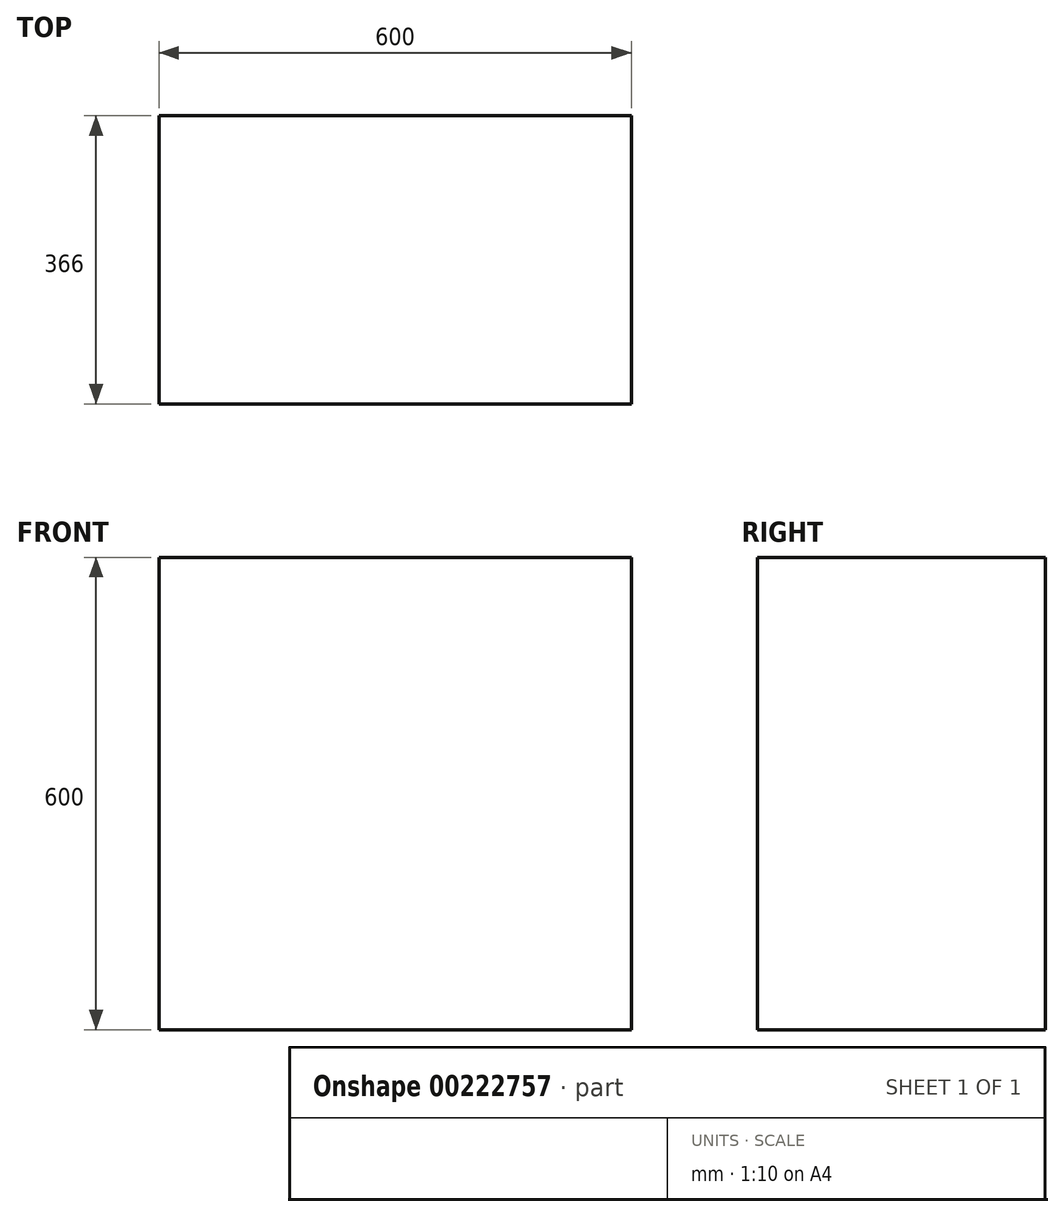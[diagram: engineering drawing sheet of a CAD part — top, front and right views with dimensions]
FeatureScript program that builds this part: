
annotation { "Feature Type Name" : "Feature", "Feature Type Description" : "" }
export const myFeature = defineFeature(function(context is Context, id is Id, definition is map)
    precondition{}
    {
        {
            var Q0;
            Q0=qCreatedBy(makeId("Top.planeOp"),FACE);
            var sketch = newSketch(context, id + "F0", { "sketchPlane" : qUnion([Q0])});
            skLineSegment(sketch, "E0.bottom", {"start": v(-302.26, 137.81) * mm, "end": v(297.74, 137.81) * mm});
            skLineSegment(sketch, "E0.top", {"start": v(-302.26, -228.19) * mm, "end": v(297.74, -228.19) * mm});
            skLineSegment(sketch, "E0.left", {"start": v(-302.26, 137.81) * mm, "end": v(-302.26, -228.19) * mm});
            skLineSegment(sketch, "E0.right", {"start": v(297.74, 137.81) * mm, "end": v(297.74, -228.19) * mm});
            skSolve(sketch);
        }
        {
            var Q0;
            Q0=makeQuery(id+"F0.imprint","IMPRINT",FACE,{"disambiguationData":[TD([[makeQuery(id+"F0.imprint","IMPRINT",EDGE,{"derivedFrom":sQuery(id+"F0.wireOp",EDGE,"E0.bottom")}),-1.0]])]});
            extrude(context, id + "F1", {"entities" : qUnion([Q0]), "depth" : 600 * mm});
        }
    });
